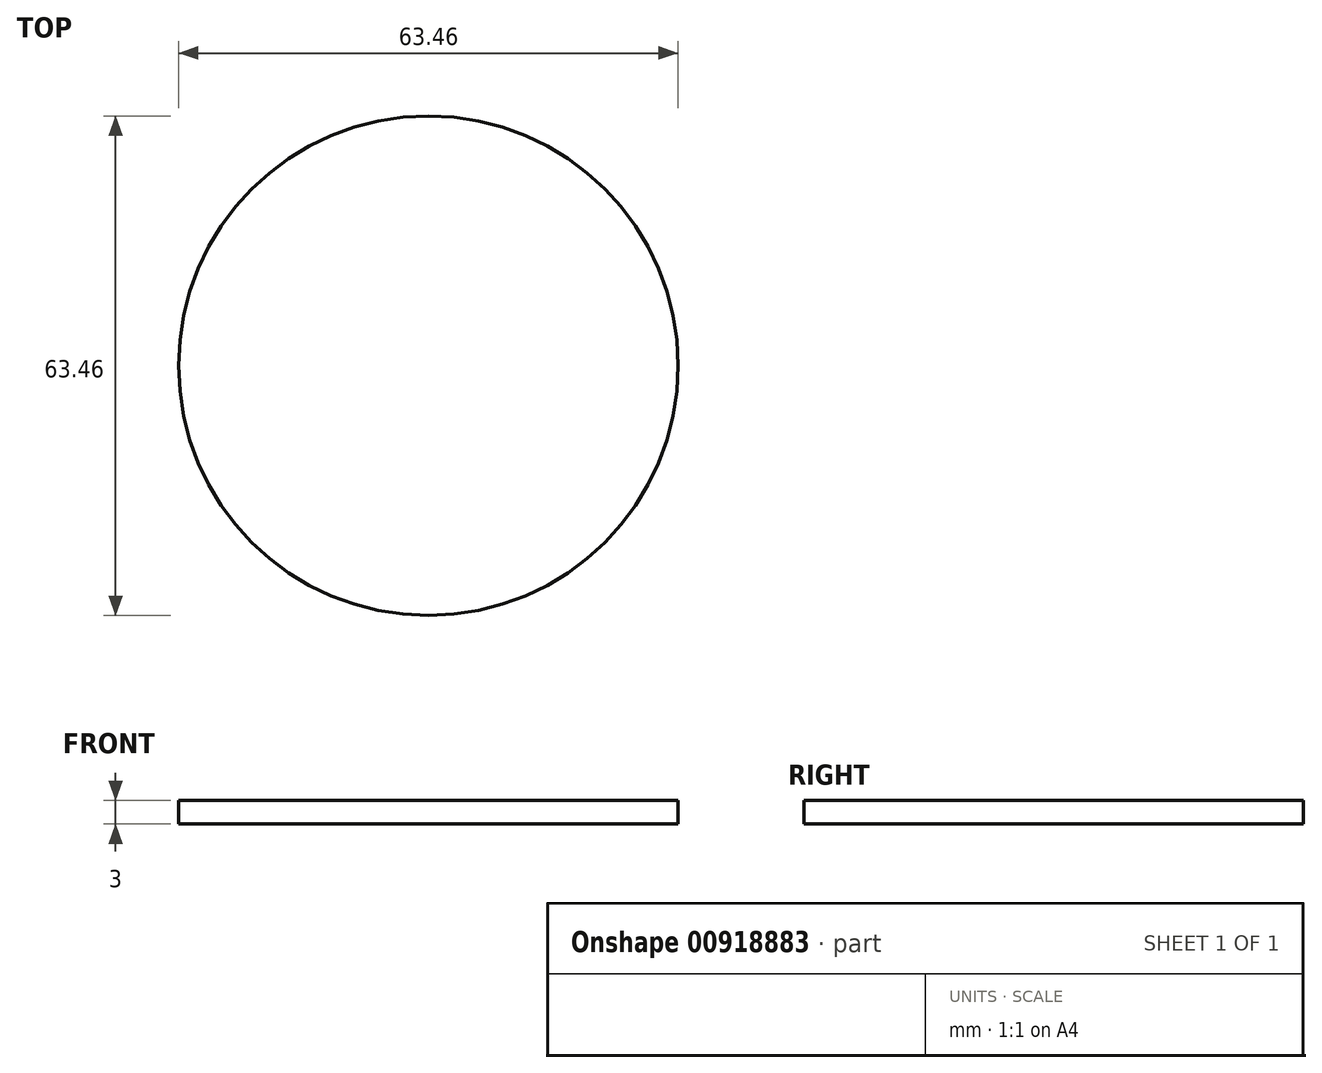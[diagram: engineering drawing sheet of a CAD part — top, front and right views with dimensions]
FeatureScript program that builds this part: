
annotation { "Feature Type Name" : "Feature", "Feature Type Description" : "" }
export const myFeature = defineFeature(function(context is Context, id is Id, definition is map)
    precondition{}
    {
        {
            var Q0;
            Q0=qCreatedBy(makeId("Top.planeOp"),FACE);
            var sketch = newSketch(context, id + "F0", { "sketchPlane" : qUnion([Q0])});
            skCircle(sketch, "E0", {"center": v(-16.24, 21.3) * mm, "radius": 31.73 * mm});
            skSolve(sketch);
        }
        {
            var Q0;
            Q0=makeQuery(id+"F0.imprint","IMPRINT",FACE,{"disambiguationData":[TD([[makeQuery(id+"F0.imprint","IMPRINT",EDGE,{"derivedFrom":sQuery(id+"F0.wireOp",EDGE,"E0")}),1.0]])]});
            extrude(context, id + "F1", {"entities" : qUnion([Q0]), "depth" : 3 * mm, "offsetDistance" : 25.4 * mm});
        }
    });
